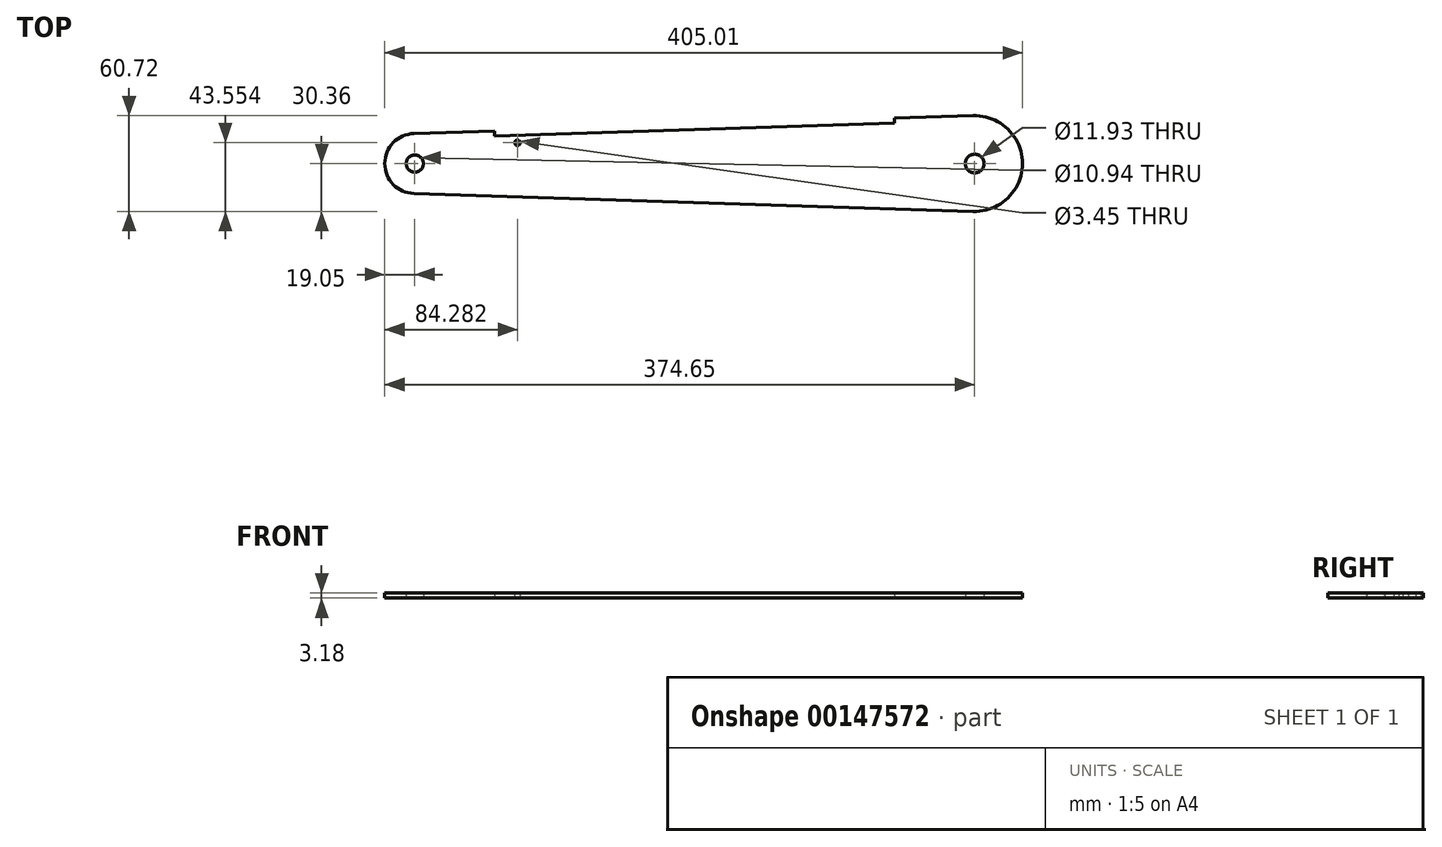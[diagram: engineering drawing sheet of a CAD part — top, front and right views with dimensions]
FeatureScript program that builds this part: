
annotation { "Feature Type Name" : "Feature", "Feature Type Description" : "" }
export const myFeature = defineFeature(function(context is Context, id is Id, definition is map)
    precondition{}
    {
        {
            var Q0;
            Q0=qCreatedBy(makeId("Top.planeOp"),FACE);
            var sketch = newSketch(context, id + "F0", { "sketchPlane" : qUnion([Q0])});
            skLineSegment(sketch, "E0", {"start": v(0, 0) * mm, "end": v(-355.6, 0) * mm, "construction": true});
            skArc(sketch, "E1", {"start": v(-0.97, -30.35) * mm, "mid": v(30.36, 0) * mm, "end": v(-0.97, 30.35) * mm});
            skArc(sketch, "E2", {"start": v(-356.2, 19.04) * mm, "mid": v(-374.65, 0) * mm, "end": v(-356.2, -19.04) * mm});
            skLineSegment(sketch, "E3", {"start": v(-356.2, -19.04) * mm, "end": v(-0.97, -30.35) * mm});
            skCircle(sketch, "E4", {"center": v(0, 0) * mm, "radius": 5.96 * mm});
            skCircle(sketch, "E5", {"center": v(-355.6, 0) * mm, "radius": 5.47 * mm});
            skLineSegment(sketch, "E6", {"start": v(-0.97, 30.35) * mm, "end": v(-51.03, 28.75) * mm});
            skLineSegment(sketch, "E7.bottom", {"start": v(-51.03, 28.75) * mm, "end": v(-304.9, 20.67) * mm, "construction": true});
            skLineSegment(sketch, "E7.top", {"start": v(-50.93, 25.58) * mm, "end": v(-304.8, 17.5) * mm});
            skLineSegment(sketch, "E7.left", {"start": v(-51.03, 28.75) * mm, "end": v(-50.93, 25.58) * mm});
            skLineSegment(sketch, "E7.right", {"start": v(-304.9, 20.67) * mm, "end": v(-304.8, 17.5) * mm});
            skLineSegment(sketch, "E8", {"start": v(-356.2, 19.04) * mm, "end": v(-304.9, 20.67) * mm});
            skLineSegment(sketch, "E9", {"start": v(-355.6, 0) * mm, "end": v(-355.6, 8.75) * mm, "construction": true});
            skLineSegment(sketch, "E10", {"start": v(-355.6, 8.75) * mm, "end": v(-304.8, 8.75) * mm, "construction": true});
            skLineSegment(sketch, "E11", {"start": v(-304.8, 8.75) * mm, "end": v(-304.8, 17.5) * mm, "construction": true});
            skLineSegment(sketch, "E12", {"start": v(-304.8, 17.5) * mm, "end": v(-304.65, 12.74) * mm, "construction": true});
            skLineSegment(sketch, "E13", {"start": v(-304.65, 12.74) * mm, "end": v(-290.37, 13.2) * mm, "construction": true});
            skCircle(sketch, "E14", {"center": v(-290.37, 13.2) * mm, "radius": 1.73 * mm});
            skSolve(sketch);
        }
        {
            var Q0;
            Q0=makeQuery(id+"F0.imprint","IMPRINT",FACE,{"disambiguationData":[TD([[makeQuery(id+"F0.imprint","IMPRINT",EDGE,{"derivedFrom":sQuery(id+"F0.wireOp",EDGE,"E1")}),1.0]])]});
            extrude(context, id + "F1", {"entities" : qUnion([Q0]), "depth" : 3.17 * mm});
        }
    });
